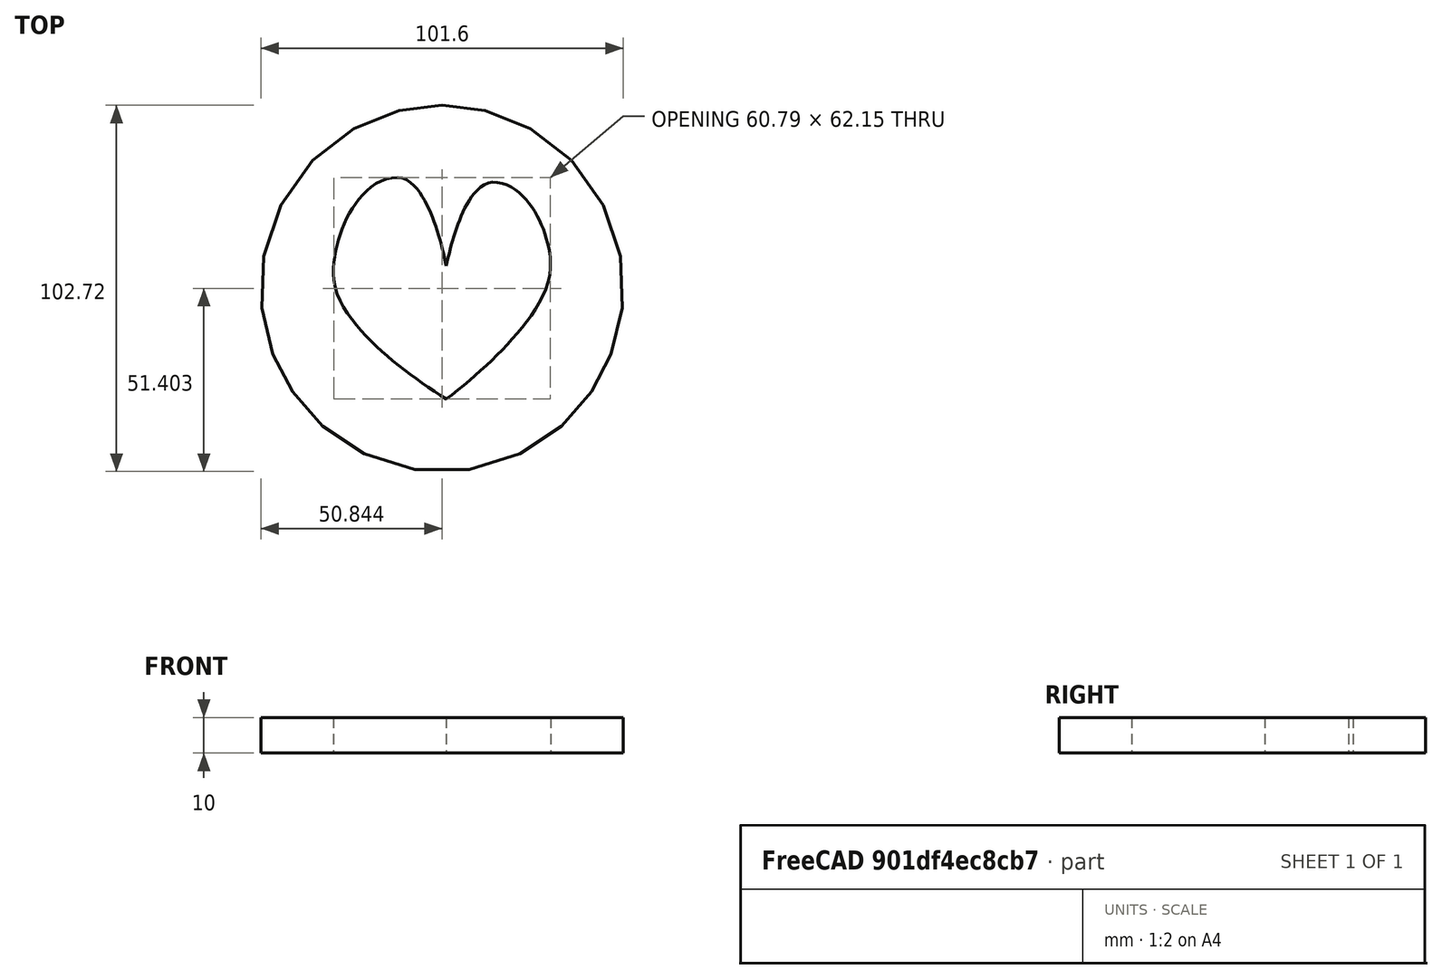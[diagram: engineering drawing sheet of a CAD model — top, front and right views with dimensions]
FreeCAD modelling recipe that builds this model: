
FCSTD DOCUMENT  (FreeCAD 1.0R38806 (Git))
Label: reto_1
License: All rights reserved
LicenseURL: https://en.wikipedia.org/wiki/All_rights_reserved
objects: Part::Feature×2, Part::Extrusion×2, Part::Cut×1
note: 5 computed .brp shape members not serialized (recipe doc carries the construction recipe); baked Part::Feature solids carry a one-line shape summary decoded from their .brp

FEATURE [Part::Feature] path1
  Placement = pos=(-43.5,-253.5,0) rot=(0,0,1;1.5708rad)
  shape: bbox 122.9 x 113.4 x 2e-07 mm, 0 faces, 0 solids (baked)
FEATURE [Part::Feature] path2
  shape: bbox 62.23 x 62.48 x 2e-07 mm, 0 faces, 0 solids (baked)
FEATURE [Part::Extrusion] Extrude
  Base = -> path1
  Dir = (0,0,1)
  DirMode = 2
  FaceMakerClass = Part::FaceMakerBullseye
  FaceMakerMode = 3
  LengthFwd = 10
  LengthRev = 0
  Solid = true
  Symmetric = false
FEATURE [Part::Extrusion] Extrude001
  Base = -> path2
  Dir = (0,0,-1)
  DirMode = 2
  FaceMakerClass = Part::FaceMakerBullseye
  FaceMakerMode = 3
  LengthFwd = 30
  LengthRev = 0
  Placement = pos=(0,0,17) rot=(0,0,1;0rad)
  Solid = true
  Symmetric = false
FEATURE [Part::Cut] Cut
  Base = -> Extrude
  Refine = true
  Tool = -> Extrude001
